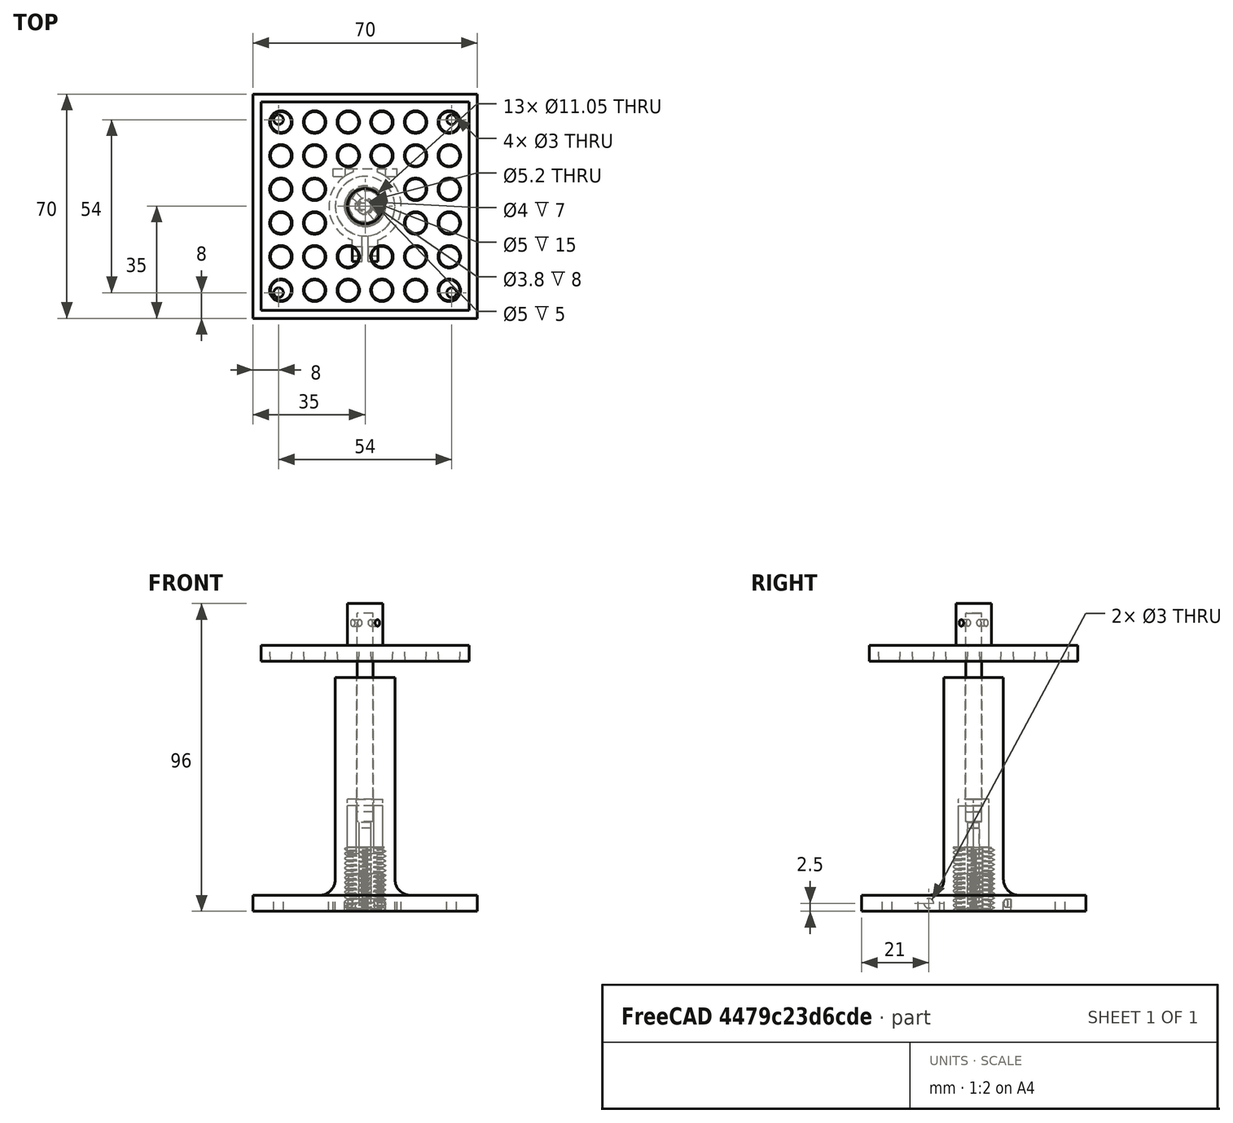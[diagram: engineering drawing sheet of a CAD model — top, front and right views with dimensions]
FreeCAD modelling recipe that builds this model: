
FCSTD DOCUMENT  (FreeCAD 0.17R13541 (Git))
Label: tip-rack
License: All rights reserved
LicenseURL: http://en.wikipedia.org/wiki/All_rights_reserved
objects: Part::Cut×52, Part::Cone×32, Part::Cylinder×27, Mesh::Feature×10, Part::Box×6, Part::MultiFuse×6, Spreadsheet::Sheet×2, Part::Helix×2, Sketcher::SketchObject×2, App::DocumentObjectGroup×2, PartDesign::FeatureBase×2, PartDesign::SubtractivePipe×2, PartDesign::Body×2, Part::Prism×2, Part::Fillet×1
note: 138 computed .brp shape members not serialized (recipe doc carries the construction recipe); baked Part::Feature solids carry a one-line shape summary decoded from their .brp

FEATURE [Spreadsheet::Sheet] Tabelle1
  cells = A1=Abstand Pip/Boden; B1=65; A3=Toleranz; B3=0.20000000000000001; A5=Teller; A6=Breite/Länge; B6=65; A7=Dicke; B7=5; A8=Befestigung höhe; B8=10; A10=Achse; A11=Durchmesser; B11=5; A12=Teller Befestigung; B12==B7 + B8; A13=Führung Länge; B13=40; C13=Wandstärke; D13=5; A14=Freiraum; B14=5; A15=Länge; B15==B14 + B13 + B12; A17=Feder; A18=Hülse durchmesser; B18=3.6000000000000001; A19=Hülse Wanddicke; B19=3; A20=L0; B20=25; A21=delta L; B21=3; A22=Spannmutter; A23=Höhe; B23=10; A24=Durchmesser Pitch; B24=20; A25=min Abstand Boden; B25=5; A28=min Oberkante Platte; B28==B25 + B23 + B20 + B19 + B13 + B7; A30=Gehäuse; A31=Wandstärke; B31=5; A32=Durchmesser; B32==B24 + 2 * B31; A33=Höhe; B33==B25 + B20 + B19 + B13; A35=Spitze d1; B35=7; A36=Spitze d2; B36=6.5; A37=Raster; B37=10.5; A38=Anzahl x/y; B38=6; A39=offset; B39==(Tabelle1.B6 - ((Tabelle1.B38 - 1) * Tabelle1.B37 + Tabelle1.B35)) / 2 + Tabelle1.B35 / 2
FEATURE [Part::Cylinder] Cylinder  label="Zylinder"
  Angle = 360
  AttacherType = Attacher::AttachEngine3D
  Height = 53
  Placement = pos=(0,0,20) rot=(0,0,1;0rad)
  Radius = 9.29904
  expr: Placement.Base.z = Spreadsheet.G1
  expr: Height = Tabelle1.B33 - Spreadsheet.G1
  expr: Radius = Spreadsheet.E5
FEATURE [Part::Cylinder] Cylinder002  label="Zylinder002"
  Angle = 360
  AttacherType = Attacher::AttachEngine3D
  Height = 50
  Placement = pos=(0,0,34.3) rot=(0,0,1;0rad)
  Radius = 2.6
  expr: Radius = Tabelle1.B11 / 2 + Tabelle1.B3 / 2
FEATURE [Part::Cylinder] Cylinder006  label="Zylinder006"
  Angle = 360
  AttacherType = Attacher::AttachEngine3D
  Height = 10
  Radius = 2.00001
  expr: Height = Tabelle1.B23
  expr: Radius = Spreadsheet.bolt_ri + 1.0000000000000001e-005
FEATURE [Part::Cylinder] Cylinder007  label="Zylinder007"
  Angle = 360
  AttacherType = Attacher::AttachEngine3D
  Height = 7
  Radius = 5.93666
  expr: Height = Tabelle1.B23 - Tabelle1.B19
  expr: Radius = Spreadsheet.bolt_ra
FEATURE [Part::Cylinder] Cylinder012  label="Zylinder012"
  Angle = 360
  AttacherType = Attacher::AttachEngine3D
  Height = 20
  Radius = 9.29904
  expr: Height = Spreadsheet.height
  expr: Radius = Spreadsheet.nut_ra
FEATURE [Spreadsheet::Sheet] Spreadsheet
  cells = A1=steigung; B1=h; D1(pitch)=1.5; F1=bauhöhe; G1(height)=20; A2=Gewindetiefe; B2=t; C2=h*cos(30°); D2(threaddepth)==pitch * cos(30); F2=helix height; G2(height_h)=25; C3=threaddepth tol; D3(threaddepth_tol)==(pitch + tolerance * cos(30)) * cos(30); F3=Flanken - Tolerance; G3(tolerance)=0; A4=Nut; F4=Radien - Tolerance; G4(tolerance_rad)=0.20000000000000001; A5=ra; E5(nut_ra)==bolt_ri + bolt_si + threaddepth + nut_sa; A6=sa; E6(nut_sa)=3; A7=ri; E7(nut_ri)==nb_centerline - threaddepth / 2 + threaddepth / 4 + tolerance_rad; A9=Bolt; A10=ri; E10(bolt_ri)==E16; A11=si; E11(bolt_si)==E17; G11==sqrt(1 / 6 ^ 2 - (tan(30) / 4) ^ 2) * Spreadsheet.threaddepth_tol; A12=ra; E12(bolt_ra)==nb_centerline + threaddepth / 2 - threaddepth / 8 - tolerance_rad; A14=Nut/Bold centerline; E14(nb_centerline)==bolt_ri + bolt_si + threaddepth / 2; A16=Spring rh; E16(spring_rh)==Tabelle1.B18 / 2 + Tabelle1.B3; A17=hülsenstärke sh; E17(spring_sh)==Tabelle1.B19; A18=join rest   js; E18(spring_sj)=1.3999999999999999; A21=join heigtht jh; B21(spring_jh)=3; A22=join ri; B22(spring_jri)==spring_rh + spring_sh + tolerance
FEATURE [Part::Cylinder] Cylinder011  label="Zylinder011"
  Angle = 360
  AttacherType = Attacher::AttachEngine3D
  Height = 20
  Radius = 5.52476
  expr: Height = Spreadsheet.height
  expr: Radius = Spreadsheet.nut_ri
FEATURE [Part::Helix] Helix004
  Angle = 0
  AttacherType = Attacher::AttachEngine3D
  Height = 25
  LocalCoord = 0
  Pitch = 1.5
  Radius = 5.52476
  Style = 1
  expr: Radius = Spreadsheet.nut_ri
  expr: Height = Spreadsheet.height_h
  expr: Pitch = Spreadsheet.pitch
FEATURE [Part::Helix] Helix003
  Angle = 0
  AttacherType = Attacher::AttachEngine3D
  Height = 25
  LocalCoord = 0
  Pitch = 1.5
  Radius = 5.93666
  Style = 1
  expr: Radius = Spreadsheet.bolt_ra
  expr: Height = Spreadsheet.height_h
  expr: Pitch = Spreadsheet.pitch
FEATURE [Sketcher::SketchObject] CopySketch001
  Placement = pos=(0,0,0) rot=(1,0,0;1.5708rad)
  expr: Constraints[5] = Spreadsheet.pitch / 2
  expr: Constraints[20] = Spreadsheet.threaddepth_tol / 12
  expr: Constraints[17] = Spreadsheet.threaddepth_tol * (1 - 1 / 4 - 1 / 8)
  expr: Constraints[16] = Spreadsheet.threaddepth_tol * (1 - 1 / 4) * sin(30) / cos(30)
  expr: Constraints[1] = Spreadsheet.nut_ri - 0.001
  sketch-geometry (7):
    g0: LineSegment [constr] StartX=0 StartY=0 StartZ=0 EndX=5.52376 EndY=0 EndZ=0
    g1: LineSegment [constr] StartX=5.52376 StartY=0 StartZ=0 EndX=5.52376 EndY=-0.75 EndZ=0
    g2: LineSegment StartX=5.52376 StartY=-0.75 StartZ=0 EndX=5.52376 EndY=-0.1875 EndZ=0
    g3: LineSegment StartX=5.52376 StartY=-0.75 StartZ=0 EndX=5.52376 EndY=-1.3125 EndZ=0
    g4: LineSegment StartX=5.52376 StartY=-1.3125 StartZ=0 EndX=6.33566 EndY=-0.84375 EndZ=0
    g5: LineSegment StartX=5.52376 StartY=-0.1875 StartZ=0 EndX=6.33566 EndY=-0.65625 EndZ=0
    g6: ArcOfCircle CenterX=6.28153 CenterY=-0.75 CenterZ=0 NormalX=0 NormalY=0 NormalZ=1 AngleXU=0 Radius=0.108253 StartAngle=5.23599 EndAngle=7.33038
  constraints (21):
    c: Horizontal(g0)
    c: DistanceX(g0,g0) = 5.52376
    c: Coincident(g-1,g0)
    c: Coincident(g1,g0)
    c: Vertical(g1)
    c: DistanceY(g1,g1) = 0.75
    c: Vertical(g2)
    c: Coincident(g3,g2)
    c: Vertical(g3)
    c: Equal(g2,g3)
    c: Coincident(g4,g3)
    c: Coincident(g5,g2)
    c: Coincident(g2,g1)
    c: Equal(g5,g4)
    c: Angle(g2,g5) = 1.0472
    c: Angle(g4,g3) = 1.0472
    c: DistanceY(g3,g3) = 0.5625
    c: DistanceX(g5,g5) = 0.811899
    c: Coincident(g6,g5)
    c: Coincident(g6,g4)
    c: Radius(g6) = 0.108253
FEATURE [Sketcher::SketchObject] CopySketch003
  Placement = pos=(0,0,0) rot=(1,0,0;1.5708rad)
  expr: Constraints[26] = Spreadsheet.threaddepth_tol * (1 - 1 / 4 - 1 / 8) - sqrt(1 / 6 ^ 2 - (tan(30) / 4) ^ 2) * Spreadsheet.threaddepth_tol
  expr: Constraints[7] = Spreadsheet.threaddepth_tol * (1 - 1 / 8) * tan(30)
  expr: Constraints[1] = Spreadsheet.bolt_ra + 0.001
  expr: Constraints[17] = Spreadsheet.pitch / 2
  expr: Constraints[20] = Spreadsheet.threaddepth_tol * (1 - 1 / 4 - 1 / 8)
  sketch-geometry (9):
    g0: LineSegment [constr] StartX=0 StartY=0 StartZ=0 EndX=5.93766 EndY=0 EndZ=0
    g1: LineSegment StartX=5.93766 StartY=-0.09375 StartZ=0 EndX=5.93766 EndY=-0.75 EndZ=0
    g2: LineSegment StartX=5.93766 StartY=-0.75 StartZ=0 EndX=5.93766 EndY=-1.40625 EndZ=0
    g3: LineSegment StartX=5.93766 StartY=-0.09375 StartZ=0 EndX=5.12576 EndY=-0.5625 EndZ=0
    g4: LineSegment StartX=5.93766 StartY=-1.40625 StartZ=0 EndX=5.12576 EndY=-0.9375 EndZ=0
    g5: LineSegment [constr] StartX=5.12576 StartY=-0.5625 StartZ=0 EndX=5.12576 EndY=-0.9375 EndZ=0
    g6: LineSegment [constr] StartX=5.93766 StartY=-0.75 StartZ=0 EndX=5.93766 EndY=0 EndZ=0
    g7: LineSegment [constr] StartX=5.93766 StartY=-0.75 StartZ=0 EndX=5.23401 EndY=-0.75 EndZ=0
    g8: ArcOfCircle CenterX=5.23401 CenterY=-0.75 CenterZ=0 NormalX=0 NormalY=0 NormalZ=1 AngleXU=0 Radius=0.216506 StartAngle=2.0944 EndAngle=4.18879
  constraints (27):
    c: Horizontal(g0)
    c: DistanceX(g0,g0) = 5.93766
    c: Coincident(g-1,g0)
    c: Vertical(g1)
    c: Coincident(g2,g1)
    c: Vertical(g2)
    c: Equal(g1,g2)
    c: DistanceY(g1,g1) = 0.65625
    c: Coincident(g3,g1)
    c: Angle(g3,g1) = 1.0472
    c: Coincident(g4,g2)
    c: Angle(g2,g4) = 1.0472
    c: Vertical(g5)
    c: Coincident(g4,g5)
    c: Equal(g4,g3)
    c: Coincident(g6,g1)
    c: Vertical(g6)
    c: DistanceY(g6,g6) = 0.75
    c: Coincident(g6,g0)
    c: Coincident(g3,g5)
    c: DistanceX(g4,g4) = 0.811899
    c: Coincident(g7,g1)
    c: Horizontal(g7)
    c: Coincident(g8,g7)
    c: Coincident(g8,g3)
    c: Coincident(g8,g4)
    c: DistanceX(g7,g7) = 0.703646
FEATURE [Part::Cut] Cut003
  Base = -> Cylinder007
  Tool = -> Cylinder006
FEATURE [Part::Cut] Cut005
  Base = -> Cylinder012
  Tool = -> Cylinder011
FEATURE [App::DocumentObjectGroup] Gruppe  label="Nut"
  Group = -> [Helix004,Cut005]
FEATURE [PartDesign::FeatureBase] BaseFeature003
  BaseFeature = -> Cut003
FEATURE [PartDesign::FeatureBase] BaseFeature004
  BaseFeature = -> Cut005
FEATURE [PartDesign::SubtractivePipe] SubtractivePipe004
  AuxilleryCurvelinear = true
  AuxillerySpineTangent = false
  BaseFeature = -> BaseFeature004
  Binormal = (0,0,0)
  Mode = 2
  Profile = -> CopySketch001
  Spine = -> Helix004 [Edge1,Edge2,Edge3,Edge4,Edge5,Edge6,Edge7,Edge8,Edge9,Edge10,Edge11,Edge12,Edge13,Edge14]
  SpineTangent = false
  Transformation = 0
  Transition = 0
FEATURE [PartDesign::Body] Body007  label="JoinNut"
  BaseFeature = -> Cut005
  Group = -> [BaseFeature004,SubtractivePipe004]
  Origin = -> Origin010
  Tip = -> SubtractivePipe004
FEATURE [PartDesign::SubtractivePipe] SubtractivePipe003
  AuxilleryCurvelinear = true
  AuxillerySpineTangent = false
  BaseFeature = -> BaseFeature003
  Binormal = (0,0,0)
  Mode = 2
  Profile = -> CopySketch003
  Spine = -> Helix003 [Edge1,Edge2,Edge3,Edge4,Edge5,Edge6,Edge7,Edge8,Edge9,Edge10,Edge11]
  SpineTangent = false
  Transformation = 0
  Transition = 0
FEATURE [PartDesign::Body] Body006  label="JoinBolt"
  BaseFeature = -> Cut003
  Group = -> [BaseFeature003,CopySketch003,SubtractivePipe003]
  Origin = -> Origin009
  Placement = pos=(0,0,4.75) rot=(0,0,1;0rad)
  Tip = -> SubtractivePipe003
  expr: Placement.Base.z = Spreadsheet.D1 / 2 + 4
FEATURE [Part::Cylinder] Cylinder013  label="Feder"
  Angle = 360
  AttacherType = Attacher::AttachEngine3D
  Height = 25
  Placement = pos=(0,0,2.75) rot=(0,0,1;0rad)
  Radius = 1.8
  expr: Placement.Base.z = Spreadsheet.D1 / 2 + 2
  expr: Height = Tabelle1.B20
  expr: Radius = Tabelle1.B18 / 2
FEATURE [Part::Cylinder] Cylinder015  label="Zylinder015"
  Angle = 360
  AttacherType = Attacher::AttachEngine3D
  Height = 4
  Placement = pos=(0,0,0.75) rot=(0,0,1;0rad)
  Radius = 5.32476
  expr: Placement.Base.z = Spreadsheet.D1 / 2
  expr: Height = 4
  expr: Radius = Spreadsheet.E7 - Tabelle1.B3
FEATURE [Part::Cylinder] Cylinder017  label="Zylinder017"
  Angle = 360
  AttacherType = Attacher::AttachEngine3D
  Height = 8
  Radius = 1.9
FEATURE [Part::Box] Box  label="Quader"
  AttacherType = Attacher::AttachEngine3D
  Height = 2
  Length = 6
  Placement = pos=(-3,-1,0.75) rot=(0,0,1;0rad)
  Width = 2
  expr: Placement.Base.z = Spreadsheet.D1 / 2
FEATURE [Part::Cut] Cut007
  Base = -> Cylinder015
  Tool = -> Box
FEATURE [Part::Box] Box001  label="Platte"
  AttacherType = Attacher::AttachEngine3D
  Height = 5
  Length = 65
  Placement = pos=(-32.5,-32.5,78) rot=(0,0,1;0rad)
  Width = 65
  expr: Length = Tabelle1.B6
  expr: Placement.Base.z = Tabelle1.B33 + Tabelle1.B14
  expr: Placement.Base.y = -Tabelle1.B6 / 2
  expr: Placement.Base.x = -Tabelle1.B6 / 2
  expr: Width = Tabelle1.B6
FEATURE [Part::Cylinder] Cylinder018  label="shaft"
  Angle = 360
  AttacherType = Attacher::AttachEngine3D
  Height = 62
  Placement = pos=(0,0,31) rot=(0,0,1;0rad)
  Radius = 2.5
  expr: Placement.Base.z = Tabelle1.B33 + Tabelle1.B14 - Tabelle1.B15 + Tabelle1.B12 - 2
  expr: Height = Tabelle1.B15 + 2
FEATURE [Part::Cylinder] Cylinder019  label="Zylinder018"
  Angle = 360
  AttacherType = Attacher::AttachEngine3D
  Height = 10
  Placement = pos=(0,0,83) rot=(0,0,1;0rad)
  Radius = 5.5
  expr: Placement.Base.z = Tabelle1.B33 + Tabelle1.B14 + Tabelle1.B7
  expr: Height = Tabelle1.B8
  expr: Radius = Tabelle1.B11 / 2 + Tabelle1.B19
FEATURE [Part::Cone] Cone  label="Kegel"
  Angle = 360
  AttacherType = Attacher::AttachEngine3D
  Height = 5
  Placement = pos=(26.25,26.25,78) rot=(0,0,1;0rad)
  Radius1 = 3.25
  Radius2 = 3.5
  expr: Placement.Base.y = Tabelle1.B6 / 2 - Tabelle1.B39
  expr: Placement.Base.x = Tabelle1.B6 / 2 - Tabelle1.B39
  expr: Placement.Base.z = Tabelle1.B33 + Tabelle1.B14
  expr: Radius2 = Tabelle1.B35 / 2
  expr: Radius1 = Tabelle1.B36 / 2
FEATURE [Part::Cone] Cone001  label="Kegel001"
  Angle = 360
  AttacherType = Attacher::AttachEngine3D
  Height = 5
  Placement = pos=(26.25,15.75,78) rot=(0,0,1;0rad)
  Radius1 = 3.25
  Radius2 = 3.5
  expr: Placement.Base.y = Tabelle1.B6 / 2 - Tabelle1.B39 - Tabelle1.B37
  expr: Placement.Base.x = Tabelle1.B6 / 2 - Tabelle1.B39
  expr: Placement.Base.z = Tabelle1.B33 + Tabelle1.B14
  expr: Radius2 = Tabelle1.B35 / 2
  expr: Radius1 = Tabelle1.B36 / 2
FEATURE [Part::Cone] Cone002  label="Kegel002"
  Angle = 360
  AttacherType = Attacher::AttachEngine3D
  Height = 5
  Placement = pos=(26.25,5.25,78) rot=(0,0,1;0rad)
  Radius1 = 3.25
  Radius2 = 3.5
  expr: Placement.Base.y = Tabelle1.B6 / 2 - Tabelle1.B39 - Tabelle1.B37 * 2
  expr: Placement.Base.x = Tabelle1.B6 / 2 - Tabelle1.B39
  expr: Placement.Base.z = Tabelle1.B33 + Tabelle1.B14
  expr: Radius2 = Tabelle1.B35 / 2
  expr: Radius1 = Tabelle1.B36 / 2
FEATURE [Part::Cone] Cone003  label="Kegel003"
  Angle = 360
  AttacherType = Attacher::AttachEngine3D
  Height = 5
  Placement = pos=(26.25,-5.25,78) rot=(0,0,1;0rad)
  Radius1 = 3.25
  Radius2 = 3.5
  expr: Placement.Base.y = Tabelle1.B6 / 2 - Tabelle1.B39 - Tabelle1.B37 * 3
  expr: Placement.Base.x = Tabelle1.B6 / 2 - Tabelle1.B39
  expr: Placement.Base.z = Tabelle1.B33 + Tabelle1.B14
  expr: Radius2 = Tabelle1.B35 / 2
  expr: Radius1 = Tabelle1.B36 / 2
FEATURE [Part::Cone] Cone004  label="Kegel004"
  Angle = 360
  AttacherType = Attacher::AttachEngine3D
  Height = 5
  Placement = pos=(15.75,-15.75,78) rot=(0,0,1;0rad)
  Radius1 = 3.25
  Radius2 = 3.5
  expr: Placement.Base.y = Tabelle1.B6 / 2 - Tabelle1.B39 - Tabelle1.B37 * 4
  expr: Placement.Base.x = Tabelle1.B6 / 2 - Tabelle1.B39 - Tabelle1.B37
  expr: Placement.Base.z = Tabelle1.B33 + Tabelle1.B14
  expr: Radius2 = Tabelle1.B35 / 2
  expr: Radius1 = Tabelle1.B36 / 2
FEATURE [Part::Cone] Cone005  label="Kegel005"
  Angle = 360
  AttacherType = Attacher::AttachEngine3D
  Height = 5
  Placement = pos=(26.25,-15.75,78) rot=(0,0,1;0rad)
  Radius1 = 3.25
  Radius2 = 3.5
  expr: Placement.Base.y = Tabelle1.B6 / 2 - Tabelle1.B37 * 4 - Tabelle1.B39
  expr: Placement.Base.x = Tabelle1.B6 / 2 - Tabelle1.B39
  expr: Placement.Base.z = Tabelle1.B33 + Tabelle1.B14
  expr: Radius2 = Tabelle1.B35 / 2
  expr: Radius1 = Tabelle1.B36 / 2
FEATURE [Part::Cone] Cone006  label="Kegel006"
  Angle = 360
  AttacherType = Attacher::AttachEngine3D
  Height = 5
  Placement = pos=(15.75,-5.25,78) rot=(0,0,1;0rad)
  Radius1 = 3.25
  Radius2 = 3.5
  expr: Placement.Base.y = Tabelle1.B6 / 2 - Tabelle1.B39 - Tabelle1.B37 * 3
  expr: Placement.Base.x = Tabelle1.B6 / 2 - Tabelle1.B39 - Tabelle1.B37
  expr: Placement.Base.z = Tabelle1.B33 + Tabelle1.B14
  expr: Radius2 = Tabelle1.B35 / 2
  expr: Radius1 = Tabelle1.B36 / 2
FEATURE [Part::Cone] Cone007  label="Kegel007"
  Angle = 360
  AttacherType = Attacher::AttachEngine3D
  Height = 5
  Placement = pos=(15.75,5.25,78) rot=(0,0,1;0rad)
  Radius1 = 3.25
  Radius2 = 3.5
  expr: Placement.Base.y = Tabelle1.B6 / 2 - Tabelle1.B39 - Tabelle1.B37 * 2
  expr: Placement.Base.x = Tabelle1.B6 / 2 - Tabelle1.B39 - Tabelle1.B37
  expr: Placement.Base.z = Tabelle1.B33 + Tabelle1.B14
  expr: Radius2 = Tabelle1.B35 / 2
  expr: Radius1 = Tabelle1.B36 / 2
FEATURE [Part::Cone] Cone008  label="Kegel008"
  Angle = 360
  AttacherType = Attacher::AttachEngine3D
  Height = 5
  Placement = pos=(15.75,15.75,78) rot=(0,0,1;0rad)
  Radius1 = 3.25
  Radius2 = 3.5
  expr: Placement.Base.y = Tabelle1.B6 / 2 - Tabelle1.B39 - Tabelle1.B37
  expr: Placement.Base.x = Tabelle1.B6 / 2 - Tabelle1.B39 - Tabelle1.B37
  expr: Placement.Base.z = Tabelle1.B33 + Tabelle1.B14
  expr: Radius2 = Tabelle1.B35 / 2
  expr: Radius1 = Tabelle1.B36 / 2
FEATURE [Part::Cone] Cone009  label="Kegel009"
  Angle = 360
  AttacherType = Attacher::AttachEngine3D
  Height = 5
  Placement = pos=(15.75,26.25,78) rot=(0,0,1;0rad)
  Radius1 = 3.25
  Radius2 = 3.5
  expr: Placement.Base.y = Tabelle1.B6 / 2 - Tabelle1.B39
  expr: Placement.Base.x = Tabelle1.B6 / 2 - Tabelle1.B39 - Tabelle1.B37
  expr: Placement.Base.z = Tabelle1.B33 + Tabelle1.B14
  expr: Radius2 = Tabelle1.B35 / 2
  expr: Radius1 = Tabelle1.B36 / 2
FEATURE [Part::Cone] Cone010  label="Kegel010"
  Angle = 360
  AttacherType = Attacher::AttachEngine3D
  Height = 5
  Placement = pos=(5.25,-15.75,78) rot=(0,0,1;0rad)
  Radius1 = 3.25
  Radius2 = 3.5
  expr: Placement.Base.y = Tabelle1.B6 / 2 - Tabelle1.B39 - Tabelle1.B37 * 4
  expr: Placement.Base.x = Tabelle1.B6 / 2 - Tabelle1.B39 - Tabelle1.B37 * 2
  expr: Placement.Base.z = Tabelle1.B33 + Tabelle1.B14
  expr: Radius2 = Tabelle1.B35 / 2
  expr: Radius1 = Tabelle1.B36 / 2
FEATURE [Part::Cone] Cone011  label="Kegel011"
  Angle = 360
  AttacherType = Attacher::AttachEngine3D
  Height = 5
  Placement = pos=(-5.25,-15.75,78) rot=(0,0,1;0rad)
  Radius1 = 3.25
  Radius2 = 3.5
  expr: Placement.Base.y = Tabelle1.B6 / 2 - Tabelle1.B39 - Tabelle1.B37 * 4
  expr: Placement.Base.x = Tabelle1.B6 / 2 - Tabelle1.B39 - Tabelle1.B37 * 3
  expr: Placement.Base.z = Tabelle1.B33 + Tabelle1.B14
  expr: Radius2 = Tabelle1.B35 / 2
  expr: Radius1 = Tabelle1.B36 / 2
FEATURE [Part::Cone] Cone012  label="Kegel012"
  Angle = 360
  AttacherType = Attacher::AttachEngine3D
  Height = 5
  Placement = pos=(-15.75,-15.75,78) rot=(0,0,1;0rad)
  Radius1 = 3.25
  Radius2 = 3.5
  expr: Placement.Base.y = Tabelle1.B6 / 2 - Tabelle1.B39 - Tabelle1.B37 * 4
  expr: Placement.Base.x = Tabelle1.B6 / 2 - Tabelle1.B39 - Tabelle1.B37 * 4
  expr: Placement.Base.z = Tabelle1.B33 + Tabelle1.B14
  expr: Radius2 = Tabelle1.B35 / 2
  expr: Radius1 = Tabelle1.B36 / 2
FEATURE [Part::Cone] Cone013  label="Kegel013"
  Angle = 360
  AttacherType = Attacher::AttachEngine3D
  Height = 5
  Placement = pos=(-15.75,-5.25,78) rot=(0,0,1;0rad)
  Radius1 = 3.25
  Radius2 = 3.5
  expr: Placement.Base.y = Tabelle1.B6 / 2 - Tabelle1.B39 - Tabelle1.B37 * 3
  expr: Placement.Base.x = Tabelle1.B6 / 2 - Tabelle1.B39 - Tabelle1.B37 * 4
  expr: Placement.Base.z = Tabelle1.B33 + Tabelle1.B14
  expr: Radius2 = Tabelle1.B35 / 2
  expr: Radius1 = Tabelle1.B36 / 2
FEATURE [Part::Cone] Cone014  label="Kegel014"
  Angle = 360
  AttacherType = Attacher::AttachEngine3D
  Height = 5
  Placement = pos=(-15.75,5.25,78) rot=(0,0,1;0rad)
  Radius1 = 3.25
  Radius2 = 3.5
  expr: Placement.Base.y = Tabelle1.B6 / 2 - Tabelle1.B39 - Tabelle1.B37 * 2
  expr: Placement.Base.x = Tabelle1.B6 / 2 - Tabelle1.B39 - Tabelle1.B37 * 4
  expr: Placement.Base.z = Tabelle1.B33 + Tabelle1.B14
  expr: Radius2 = Tabelle1.B35 / 2
  expr: Radius1 = Tabelle1.B36 / 2
FEATURE [Part::Cone] Cone015  label="Kegel015"
  Angle = 360
  AttacherType = Attacher::AttachEngine3D
  Height = 5
  Placement = pos=(-15.75,15.75,78) rot=(0,0,1;0rad)
  Radius1 = 3.25
  Radius2 = 3.5
  expr: Placement.Base.y = Tabelle1.B6 / 2 - Tabelle1.B39 - Tabelle1.B37
  expr: Placement.Base.x = Tabelle1.B6 / 2 - Tabelle1.B39 - Tabelle1.B37 * 4
  expr: Placement.Base.z = Tabelle1.B33 + Tabelle1.B14
  expr: Radius2 = Tabelle1.B35 / 2
  expr: Radius1 = Tabelle1.B36 / 2
FEATURE [Part::Cone] Cone016  label="Kegel016"
  Angle = 360
  AttacherType = Attacher::AttachEngine3D
  Height = 5
  Placement = pos=(-15.75,26.25,78) rot=(0,0,1;0rad)
  Radius1 = 3.25
  Radius2 = 3.5
  expr: Placement.Base.y = Tabelle1.B6 / 2 - Tabelle1.B39
  expr: Placement.Base.x = Tabelle1.B6 / 2 - Tabelle1.B39 - Tabelle1.B37 * 4
  expr: Placement.Base.z = Tabelle1.B33 + Tabelle1.B14
  expr: Radius2 = Tabelle1.B35 / 2
  expr: Radius1 = Tabelle1.B36 / 2
FEATURE [Part::Cone] Cone017  label="Kegel017"
  Angle = 360
  AttacherType = Attacher::AttachEngine3D
  Height = 5
  Placement = pos=(-5.25,26.25,78) rot=(0,0,1;0rad)
  Radius1 = 3.25
  Radius2 = 3.5
  expr: Placement.Base.y = Tabelle1.B6 / 2 - Tabelle1.B39
  expr: Placement.Base.x = Tabelle1.B6 / 2 - Tabelle1.B39 - Tabelle1.B37 * 3
  expr: Placement.Base.z = Tabelle1.B33 + Tabelle1.B14
  expr: Radius2 = Tabelle1.B35 / 2
  expr: Radius1 = Tabelle1.B36 / 2
FEATURE [Part::Cone] Cone018  label="Kegel018"
  Angle = 360
  AttacherType = Attacher::AttachEngine3D
  Height = 5
  Placement = pos=(5.25,26.25,78) rot=(0,0,1;0rad)
  Radius1 = 3.25
  Radius2 = 3.5
  expr: Placement.Base.y = Tabelle1.B6 / 2 - Tabelle1.B39
  expr: Placement.Base.x = Tabelle1.B6 / 2 - Tabelle1.B39 - Tabelle1.B37 * 2
  expr: Placement.Base.z = Tabelle1.B33 + Tabelle1.B14
  expr: Radius2 = Tabelle1.B35 / 2
  expr: Radius1 = Tabelle1.B36 / 2
FEATURE [Part::Cone] Cone019  label="Kegel019"
  Angle = 360
  AttacherType = Attacher::AttachEngine3D
  Height = 5
  Placement = pos=(-5.25,15.75,78) rot=(0,0,1;0rad)
  Radius1 = 3.25
  Radius2 = 3.5
  expr: Placement.Base.y = Tabelle1.B6 / 2 - Tabelle1.B39 - Tabelle1.B37
  expr: Placement.Base.x = Tabelle1.B6 / 2 - Tabelle1.B39 - Tabelle1.B37 * 3
  expr: Placement.Base.z = Tabelle1.B33 + Tabelle1.B14
  expr: Radius2 = Tabelle1.B35 / 2
  expr: Radius1 = Tabelle1.B36 / 2
FEATURE [Part::Cone] Cone020  label="Kegel020"
  Angle = 360
  AttacherType = Attacher::AttachEngine3D
  Height = 5
  Placement = pos=(5.25,15.75,78) rot=(0,0,1;0rad)
  Radius1 = 3.25
  Radius2 = 3.5
  expr: Placement.Base.y = Tabelle1.B6 / 2 - Tabelle1.B39 - Tabelle1.B37
  expr: Placement.Base.x = Tabelle1.B6 / 2 - Tabelle1.B39 - Tabelle1.B37 * 2
  expr: Placement.Base.z = Tabelle1.B33 + Tabelle1.B14
  expr: Radius2 = Tabelle1.B35 / 2
  expr: Radius1 = Tabelle1.B36 / 2
FEATURE [Part::Cone] Cone021  label="Kegel021"
  Angle = 360
  AttacherType = Attacher::AttachEngine3D
  Height = 5
  Placement = pos=(5.25,-26.25,78) rot=(0,0,1;0rad)
  Radius1 = 3.25
  Radius2 = 3.5
  expr: Placement.Base.y = Tabelle1.B6 / 2 - Tabelle1.B39 - Tabelle1.B37 * 5
  expr: Placement.Base.x = Tabelle1.B6 / 2 - Tabelle1.B39 - Tabelle1.B37 * 2
  expr: Placement.Base.z = Tabelle1.B33 + Tabelle1.B14
  expr: Radius2 = Tabelle1.B35 / 2
  expr: Radius1 = Tabelle1.B36 / 2
FEATURE [Part::Cone] Cone022  label="Kegel022"
  Angle = 360
  AttacherType = Attacher::AttachEngine3D
  Height = 5
  Placement = pos=(15.75,-26.25,78) rot=(0,0,1;0rad)
  Radius1 = 3.25
  Radius2 = 3.5
  expr: Placement.Base.y = Tabelle1.B6 / 2 - Tabelle1.B39 - Tabelle1.B37 * 5
  expr: Placement.Base.x = Tabelle1.B6 / 2 - Tabelle1.B39 - Tabelle1.B37 * 1
  expr: Placement.Base.z = Tabelle1.B33 + Tabelle1.B14
  expr: Radius2 = Tabelle1.B35 / 2
  expr: Radius1 = Tabelle1.B36 / 2
FEATURE [Part::Cone] Cone023  label="Kegel023"
  Angle = 360
  AttacherType = Attacher::AttachEngine3D
  Height = 5
  Placement = pos=(26.25,-26.25,78) rot=(0,0,1;0rad)
  Radius1 = 3.25
  Radius2 = 3.5
  expr: Placement.Base.y = Tabelle1.B6 / 2 - Tabelle1.B39 - Tabelle1.B37 * 5
  expr: Placement.Base.x = Tabelle1.B6 / 2 - Tabelle1.B39 - Tabelle1.B37 * 0
  expr: Placement.Base.z = Tabelle1.B33 + Tabelle1.B14
  expr: Radius2 = Tabelle1.B35 / 2
  expr: Radius1 = Tabelle1.B36 / 2
FEATURE [Part::Cut] Cut008
  Base = -> Box001
  Tool = -> Cone
FEATURE [Part::Cut] Cut009
  Base = -> Cut008
  Tool = -> Cone023
FEATURE [Part::Cut] Cut010
  Base = -> Cut009
  Tool = -> Cone022
FEATURE [Part::Cut] Cut011
  Base = -> Cut010
  Tool = -> Cone021
FEATURE [Part::Cut] Cut012
  Base = -> Cut011
  Tool = -> Cone020
FEATURE [Part::Cut] Cut013
  Base = -> Cut012
  Tool = -> Cone019
FEATURE [Part::Cut] Cut014
  Base = -> Cut013
  Tool = -> Cone018
FEATURE [Part::Cut] Cut015
  Base = -> Cut014
  Tool = -> Cone017
FEATURE [Part::Cut] Cut016
  Base = -> Cut015
  Tool = -> Cone016
FEATURE [Part::Cut] Cut017
  Base = -> Cut016
  Tool = -> Cone015
FEATURE [Part::Cut] Cut018
  Base = -> Cut017
  Tool = -> Cone014
FEATURE [Part::Cut] Cut019
  Base = -> Cut018
  Tool = -> Cone013
FEATURE [Part::Cut] Cut020
  Base = -> Cut019
  Tool = -> Cone012
FEATURE [Part::Cut] Cut021
  Base = -> Cut020
  Tool = -> Cone011
FEATURE [Part::Cut] Cut022
  Base = -> Cut021
  Tool = -> Cone010
FEATURE [Part::Cut] Cut023
  Base = -> Cut022
  Tool = -> Cone009
FEATURE [Part::Cut] Cut024
  Base = -> Cut023
  Tool = -> Cone008
FEATURE [Part::Cut] Cut025
  Base = -> Cut024
  Tool = -> Cone007
FEATURE [Part::Cut] Cut026
  Base = -> Cut025
  Tool = -> Cone006
FEATURE [Part::Cut] Cut027
  Base = -> Cut026
  Tool = -> Cone005
FEATURE [Part::Cut] Cut028
  Base = -> Cut027
  Tool = -> Cone004
FEATURE [Part::Cut] Cut029
  Base = -> Cut028
  Tool = -> Cone003
FEATURE [Part::Cut] Cut030
  Base = -> Cut029
  Tool = -> Cone002
FEATURE [Part::Cut] Cut031
  Base = -> Cut030
  Tool = -> Cone001
FEATURE [Part::Cylinder] Cylinder020  label="Spindel001"
  Angle = 360
  AttacherType = Attacher::AttachEngine3D
  Height = 60
  Placement = pos=(0,0,33) rot=(0,0,1;0rad)
  Radius = 2.5
  expr: Placement.Base.z = Tabelle1.B33 + Tabelle1.B14 - Tabelle1.B15 + Tabelle1.B12
  expr: Height = Tabelle1.B15
FEATURE [Part::MultiFuse] Fusion
  Shapes = -> [Cut031,Cylinder019]
FEATURE [Part::Cut] Cut032
  Base = -> Fusion
  Tool = -> Cylinder020
FEATURE [Part::Box] Box002  label="Quader001"
  AttacherType = Attacher::AttachEngine3D
  Height = 5
  Length = 70
  Placement = pos=(-35,-35,0) rot=(0,0,1;0rad)
  Width = 70
  expr: Placement.Base.x = -70 / 2
  expr: Placement.Base.y = -70 / 2
FEATURE [Part::Cylinder] Cylinder021  label="Zylinder019"
  Angle = 360
  AttacherType = Attacher::AttachEngine3D
  Height = 10
  Radius = 9.29904
  expr: Radius = Spreadsheet.E5
FEATURE [Part::Cut] Cut033
  Base = -> Box002
  Tool = -> Cylinder021
FEATURE [Part::Cylinder] Cylinder022  label="Zylinder020"
  Angle = 360
  AttacherType = Attacher::AttachEngine3D
  Height = 5
  Placement = pos=(0,0,10) rot=(0,0,1;0rad)
  Radius = 2.5
FEATURE [Mesh::Feature] Mesh002  label="Bolt001"
FEATURE [Part::Cylinder] Cylinder023  label="Zylinder021"
  Angle = 360
  AttacherType = Attacher::AttachEngine3D
  Height = 10
  Placement = pos=(-27,-27,0) rot=(0,0,1;0rad)
  Radius = 1.5
FEATURE [Part::Cylinder] Cylinder024  label="Zylinder022"
  Angle = 360
  AttacherType = Attacher::AttachEngine3D
  Height = 10
  Placement = pos=(-27,27,0) rot=(0,0,1;0rad)
  Radius = 1.5
FEATURE [Part::Cylinder] Cylinder025  label="Zylinder023"
  Angle = 360
  AttacherType = Attacher::AttachEngine3D
  Height = 10
  Placement = pos=(27,-27,0) rot=(0,0,1;0rad)
  Radius = 1.5
FEATURE [Part::Cylinder] Cylinder026  label="Zylinder024"
  Angle = 360
  AttacherType = Attacher::AttachEngine3D
  Height = 10
  Placement = pos=(27,27,0) rot=(0,0,1;0rad)
  Radius = 1.5
FEATURE [Part::Prism] Prism  label="Prisma"
  AttacherType = Attacher::AttachEngine3D
  Circumradius = 5.47476
  Height = 15
  Polygon = 6
  expr: Circumradius = Spreadsheet.nut_ri - 0.050000000000000003
FEATURE [Part::Cut] Cut039
  Base = -> Prism
  Tool = -> Cylinder022
FEATURE [Part::Cut] Cut040  label="shaft-fixer"
  Base = -> Cut039
  Placement = pos=(0,0,18) rot=(0,0,1;0rad)
  Tool = -> Cylinder017
FEATURE [Part::Prism] Prism001  label="Prisma001"
  AttacherType = Attacher::AttachEngine3D
  Circumradius = 5.52476
  Height = 15
  Placement = pos=(0,0,20) rot=(0,0,1;0rad)
  Polygon = 6
  expr: Circumradius = Spreadsheet.nut_ri
FEATURE [Part::Cylinder] Cylinder027  label="Zylinder025"
  Angle = 360
  AttacherType = Attacher::AttachEngine3D
  Height = 3
  Placement = pos=(0,0,93) rot=(0,0,1;0rad)
  Radius = 5.5
FEATURE [Part::MultiFuse] Fusion002  label="top"
  Shapes = -> [Cut032,Cylinder027]
FEATURE [Part::Cylinder] Cylinder028  label="Zylinder026"
  Angle = 360
  AttacherType = Attacher::AttachEngine3D
  Height = 15
  Placement = pos=(-6,6,90) rot=(0.862856,0.357407,0.357407;1.71777rad)
  Radius = 1
FEATURE [Part::Cut] Cut042  label="Top"
  Base = -> Fusion002
  Tool = -> Cylinder028
FEATURE [Mesh::Feature] Mesh003  label="Top (Meshed)"
FEATURE [Mesh::Feature] Mesh004  label="Verbindung001"
FEATURE [Part::Box] Box003  label="Quader002"
  AttacherType = Attacher::AttachEngine3D
  Height = 5
  Length = 20
  Placement = pos=(-10,9.29904,0) rot=(0,0,1;0rad)
  Width = 2.4
  expr: Placement.Base.y = +Spreadsheet.E5
FEATURE [Part::Cylinder] Cylinder029  label="Zylinder027"
  Angle = 360
  AttacherType = Attacher::AttachEngine3D
  Height = 10
  Radius = 9.29904
  expr: Radius = Spreadsheet.E5
FEATURE [Part::Cylinder] Cylinder030  label="Zylinder028"
  Angle = 360
  AttacherType = Attacher::AttachEngine3D
  Height = 5
  Radius = 11.299
  expr: Radius = Spreadsheet.E5 + 2
FEATURE [Part::Cut] Cut043
  Base = -> Cylinder030
  Tool = -> Cylinder029
FEATURE [Part::Cylinder] Cylinder031  label="Zylinder029"
  Angle = 360
  AttacherType = Attacher::AttachEngine3D
  Height = 5
  Placement = pos=(5,14,2.5) rot=(1,0,0;1.5708rad)
  Radius = 1.25
FEATURE [Part::Cylinder] Cylinder032  label="Zylinder030"
  Angle = 360
  AttacherType = Attacher::AttachEngine3D
  Height = 5
  Placement = pos=(-5,14,2.5) rot=(1,0,0;1.5708rad)
  Radius = 1.25
FEATURE [Part::Cut] Cut044
  Base = -> Box003
  Tool = -> Cylinder031
FEATURE [Part::Cut] Cut045
  Base = -> Cut044
  Tool = -> Cylinder032
FEATURE [Part::Box] Box004  label="Quader003"
  AttacherType = Attacher::AttachEngine3D
  Height = 5
  Length = 8
  Placement = pos=(-4,-17.299,0) rot=(0,0,1;0rad)
  Width = 8
  expr: Placement.Base.y = -Spreadsheet.E5 - 5 - 3
FEATURE [Part::Cylinder] Cylinder033  label="Zylinder031"
  Angle = 360
  AttacherType = Attacher::AttachEngine3D
  Height = 10
  Placement = pos=(-5,-14,2.5) rot=(0,1,0;1.5708rad)
  Radius = 1.5
FEATURE [Part::Cut] Cut046
  Base = -> Box004
  Tool = -> Cylinder033
FEATURE [Part::Box] Box005  label="Quader004"
  AttacherType = Attacher::AttachEngine3D
  Height = 10
  Length = 2
  Placement = pos=(-1,-19,-1) rot=(0,0,1;0rad)
  Width = 10
FEATURE [Part::MultiFuse] Fusion003
  Shapes = -> [Cut046,Cut043,Cut045]
FEATURE [Part::Cut] Cut047  label="Endschalter"
  Base = -> Fusion003
  Tool = -> Box005
FEATURE [Mesh::Feature] Mesh  label="Endschalter (Meshed)"
FEATURE [Part::Cone] Cone024  label="Kegel024"
  Angle = 360
  AttacherType = Attacher::AttachEngine3D
  Height = 5
  Placement = pos=(-5.25,-26.25,78) rot=(0,0,1;0rad)
  Radius1 = 3.25
  Radius2 = 3.5
  expr: Placement.Base.y = Tabelle1.B6 / 2 - Tabelle1.B39 - Tabelle1.B37 * 5
  expr: Placement.Base.x = Tabelle1.B6 / 2 - Tabelle1.B39 - Tabelle1.B37 * 3
  expr: Placement.Base.z = Tabelle1.B33 + Tabelle1.B14
  expr: Radius2 = Tabelle1.B35 / 2
  expr: Radius1 = Tabelle1.B36 / 2
FEATURE [Part::Cone] Cone025  label="Kegel025"
  Angle = 360
  AttacherType = Attacher::AttachEngine3D
  Height = 5
  Placement = pos=(-15.75,-26.25,78) rot=(0,0,1;0rad)
  Radius1 = 3.25
  Radius2 = 3.5
  expr: Placement.Base.y = Tabelle1.B6 / 2 - Tabelle1.B39 - Tabelle1.B37 * 5
  expr: Placement.Base.x = Tabelle1.B6 / 2 - Tabelle1.B39 - Tabelle1.B37 * 4
  expr: Placement.Base.z = Tabelle1.B33 + Tabelle1.B14
  expr: Radius2 = Tabelle1.B35 / 2
  expr: Radius1 = Tabelle1.B36 / 2
FEATURE [Part::Cone] Cone026  label="Kegel026"
  Angle = 360
  AttacherType = Attacher::AttachEngine3D
  Height = 5
  Placement = pos=(-26.25,-26.25,78) rot=(0,0,1;0rad)
  Radius1 = 3.25
  Radius2 = 3.5
  expr: Placement.Base.y = Tabelle1.B6 / 2 - Tabelle1.B39 - Tabelle1.B37 * 5
  expr: Placement.Base.x = Tabelle1.B6 / 2 - Tabelle1.B39 - Tabelle1.B37 * 5
  expr: Placement.Base.z = Tabelle1.B33 + Tabelle1.B14
  expr: Radius2 = Tabelle1.B35 / 2
  expr: Radius1 = Tabelle1.B36 / 2
FEATURE [Part::Cone] Cone027  label="Kegel027"
  Angle = 360
  AttacherType = Attacher::AttachEngine3D
  Height = 5
  Placement = pos=(-26.25,-15.75,78) rot=(0,0,1;0rad)
  Radius1 = 3.25
  Radius2 = 3.5
  expr: Placement.Base.y = Tabelle1.B6 / 2 - Tabelle1.B39 - Tabelle1.B37 * 4
  expr: Placement.Base.x = Tabelle1.B6 / 2 - Tabelle1.B39 - Tabelle1.B37 * 5
  expr: Placement.Base.z = Tabelle1.B33 + Tabelle1.B14
  expr: Radius2 = Tabelle1.B35 / 2
  expr: Radius1 = Tabelle1.B36 / 2
FEATURE [Part::Cone] Cone028  label="Kegel028"
  Angle = 360
  AttacherType = Attacher::AttachEngine3D
  Height = 5
  Placement = pos=(-26.25,-5.25,78) rot=(0,0,1;0rad)
  Radius1 = 3.25
  Radius2 = 3.5
  expr: Placement.Base.y = Tabelle1.B6 / 2 - Tabelle1.B39 - Tabelle1.B37 * 3
  expr: Placement.Base.x = Tabelle1.B6 / 2 - Tabelle1.B39 - Tabelle1.B37 * 5
  expr: Placement.Base.z = Tabelle1.B33 + Tabelle1.B14
  expr: Radius2 = Tabelle1.B35 / 2
  expr: Radius1 = Tabelle1.B36 / 2
FEATURE [Part::Cone] Cone029  label="Kegel029"
  Angle = 360
  AttacherType = Attacher::AttachEngine3D
  Height = 5
  Placement = pos=(-26.25,5.25,78) rot=(0,0,1;0rad)
  Radius1 = 3.25
  Radius2 = 3.5
  expr: Placement.Base.y = Tabelle1.B6 / 2 - Tabelle1.B39 - Tabelle1.B37 * 2
  expr: Placement.Base.x = Tabelle1.B6 / 2 - Tabelle1.B39 - Tabelle1.B37 * 5
  expr: Placement.Base.z = Tabelle1.B33 + Tabelle1.B14
  expr: Radius2 = Tabelle1.B35 / 2
  expr: Radius1 = Tabelle1.B36 / 2
FEATURE [Part::Cone] Cone030  label="Kegel030"
  Angle = 360
  AttacherType = Attacher::AttachEngine3D
  Height = 5
  Placement = pos=(-26.25,15.75,78) rot=(0,0,1;0rad)
  Radius1 = 3.25
  Radius2 = 3.5
  expr: Placement.Base.y = Tabelle1.B6 / 2 - Tabelle1.B39 - Tabelle1.B37 * 1
  expr: Placement.Base.x = Tabelle1.B6 / 2 - Tabelle1.B39 - Tabelle1.B37 * 5
  expr: Placement.Base.z = Tabelle1.B33 + Tabelle1.B14
  expr: Radius2 = Tabelle1.B35 / 2
  expr: Radius1 = Tabelle1.B36 / 2
FEATURE [Part::Cone] Cone031  label="Kegel031"
  Angle = 360
  AttacherType = Attacher::AttachEngine3D
  Height = 5
  Placement = pos=(-26.25,26.25,78) rot=(0,0,1;0rad)
  Radius1 = 3.25
  Radius2 = 3.5
  expr: Placement.Base.y = Tabelle1.B6 / 2 - Tabelle1.B39 - Tabelle1.B37 * 0
  expr: Placement.Base.x = Tabelle1.B6 / 2 - Tabelle1.B39 - Tabelle1.B37 * 5
  expr: Placement.Base.z = Tabelle1.B33 + Tabelle1.B14
  expr: Radius2 = Tabelle1.B35 / 2
  expr: Radius1 = Tabelle1.B36 / 2
FEATURE [Part::Cut] Cut048
  Base = -> Cut042
  Tool = -> Cone024
FEATURE [Part::Cut] Cut049
  Base = -> Cut048
  Tool = -> Cone031
FEATURE [Part::Cut] Cut050
  Base = -> Cut049
  Tool = -> Cone030
FEATURE [Part::Cut] Cut051
  Base = -> Cut050
  Tool = -> Cone029
FEATURE [Part::Cut] Cut052
  Base = -> Cut051
  Tool = -> Cone028
FEATURE [Part::Cut] Cut053
  Base = -> Cut052
  Tool = -> Cone027
FEATURE [Part::Cut] Cut054
  Base = -> Cut053
  Tool = -> Cone026
FEATURE [Part::Cut] Cut055  label="top001"
  Base = -> Cut054
  Tool = -> Cone025
FEATURE [Mesh::Feature] Mesh005  label="top001 (Meshed)"
FEATURE [Mesh::Feature] Mesh006  label="top001 (Meshed)001"
FEATURE [Part::Cylinder] Cylinder034  label="Zylinder032"
  Angle = 360
  AttacherType = Attacher::AttachEngine3D
  Height = 20
  Radius = 9.29904
  expr: Radius = Spreadsheet.nut_ra
FEATURE [Part::Cylinder] Cylinder035  label="Zylinder033"
  Angle = 360
  AttacherType = Attacher::AttachEngine3D
  Height = 20
  Radius = 9.09904
  expr: Radius = Spreadsheet.nut_ra - 0.20000000000000001
FEATURE [Part::Cut] Cut056
  Base = -> Cylinder034
  Tool = -> Cylinder035
FEATURE [Part::MultiFuse] Fusion004
  Shapes = -> [Cut033,Cut056]
FEATURE [Part::Cut] Cut057
  Base = -> Fusion004
  Tool = -> Cylinder023
FEATURE [Part::Cut] Cut058
  Base = -> Cut057
  Tool = -> Cylinder024
FEATURE [Part::Cut] Cut059
  Base = -> Cut058
  Tool = -> Cylinder025
FEATURE [Part::Cut] Cut060
  Base = -> Cut059
  Tool = -> Cylinder026
FEATURE [Part::Fillet] Fillet
  Base = -> Cut060
  Edges = 1 edges r=5: [Edge12]
FEATURE [Mesh::Feature] Mesh007  label="JoinNut (Meshed)"
FEATURE [Mesh::Feature] Mesh008  label="Fillet (Meshed)"
FEATURE [Mesh::Feature] Mesh012  label="Cut041 (Meshed)"
FEATURE [Mesh::Feature] Mesh013
FEATURE [Part::MultiFuse] Fusion006
  Shapes = -> [Cut007,Body006]
FEATURE [App::DocumentObjectGroup] Gruppe001  label="Bolt"
  Group = -> [Helix003,Cut003,Fusion006]
FEATURE [Part::Cut] Cut
  Base = -> Cylinder
  Tool = -> Prism001
FEATURE [Part::Cut] Cut061
  Base = -> Cut
  Tool = -> Cylinder002
FEATURE [Part::MultiFuse] Fusion007
  Shapes = -> [Body007,Cut061,Fillet]
